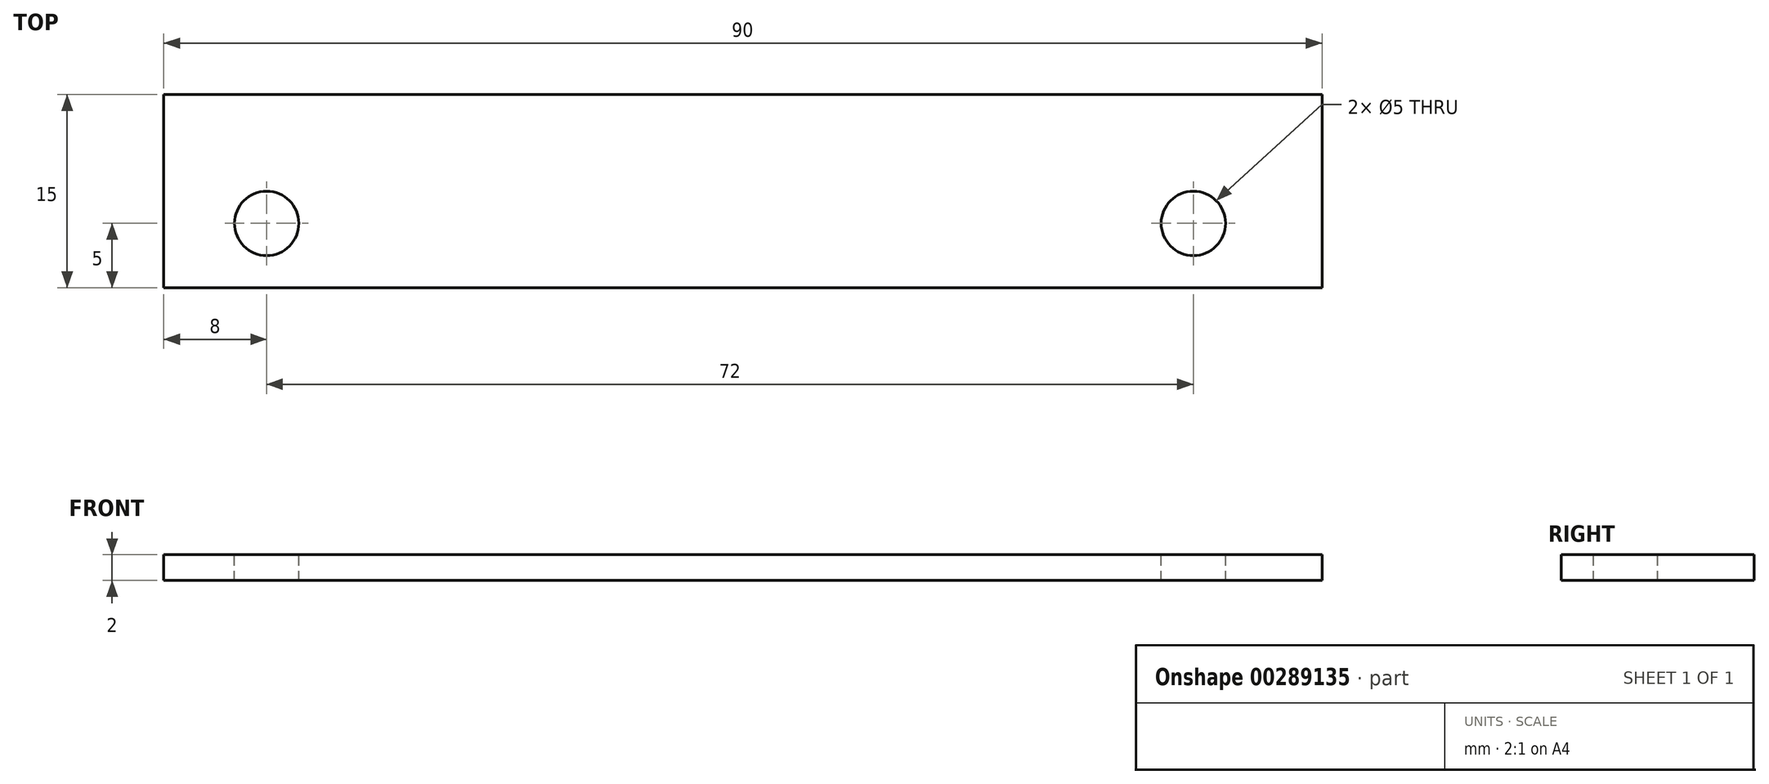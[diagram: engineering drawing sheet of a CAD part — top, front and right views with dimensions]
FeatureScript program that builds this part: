
annotation { "Feature Type Name" : "Feature", "Feature Type Description" : "" }
export const myFeature = defineFeature(function(context is Context, id is Id, definition is map)
    precondition{}
    {
        {
            var Q0;
            Q0=qCreatedBy(makeId("Top.planeOp"),FACE);
            var sketch = newSketch(context, id + "F0", { "sketchPlane" : qUnion([Q0])});
            skLineSegment(sketch, "E0.bottom", {"start": v(0, 0) * mm, "end": v(90, 0) * mm});
            skLineSegment(sketch, "E0.top", {"start": v(0, 15) * mm, "end": v(90, 15) * mm});
            skLineSegment(sketch, "E0.left", {"start": v(0, 0) * mm, "end": v(0, 15) * mm});
            skLineSegment(sketch, "E0.right", {"start": v(90, 0) * mm, "end": v(90, 15) * mm});
            skSolve(sketch);
        }
        {
            var Q0;
            Q0 = qSketchRegion(id + "F0", true);
            extrude(context, id + "F1", {"entities" : qUnion([Q0]), "depth" : 2 * mm});
        }
        {
            var Q0;
            Q0=makeQuery(id+"F1.opExtrude","CAP_FACE",FACE,{"disambiguationData":[OSD([sQuery(id+"F0.wireOp",EDGE,"E0.bottom"),sQuery(id+"F0.wireOp",EDGE,"E0.top"),sQuery(id+"F0.wireOp",EDGE,"E0.left"),sQuery(id+"F0.wireOp",EDGE,"E0.right")])],"isStart":false});
            var sketch = newSketch(context, id + "F2", { "sketchPlane" : qUnion([Q0])});
            skCircle(sketch, "E1", {"center": v(80, 5) * mm, "radius": 2.5 * mm});
            skCircle(sketch, "E2.1.0.0", {"center": v(8, 5) * mm, "radius": 2.5 * mm});
            skLineSegment(sketch, "E2.direction1", {"start": v(80, 5) * mm, "end": v(8, 5) * mm, "construction": true});
            skSolve(sketch);
        }
        {
            var Q0;
            Q0 = qSketchRegion(id + "F2", true);
            extrude(context, id + "F3", {"entities" : qUnion([Q0]), "operationType" : NewBodyOperationType.REMOVE, "endBound" : BoundingType.THROUGH_ALL, "oppositeDirection" : true, "depth" : 25 * mm});
        }
    });
